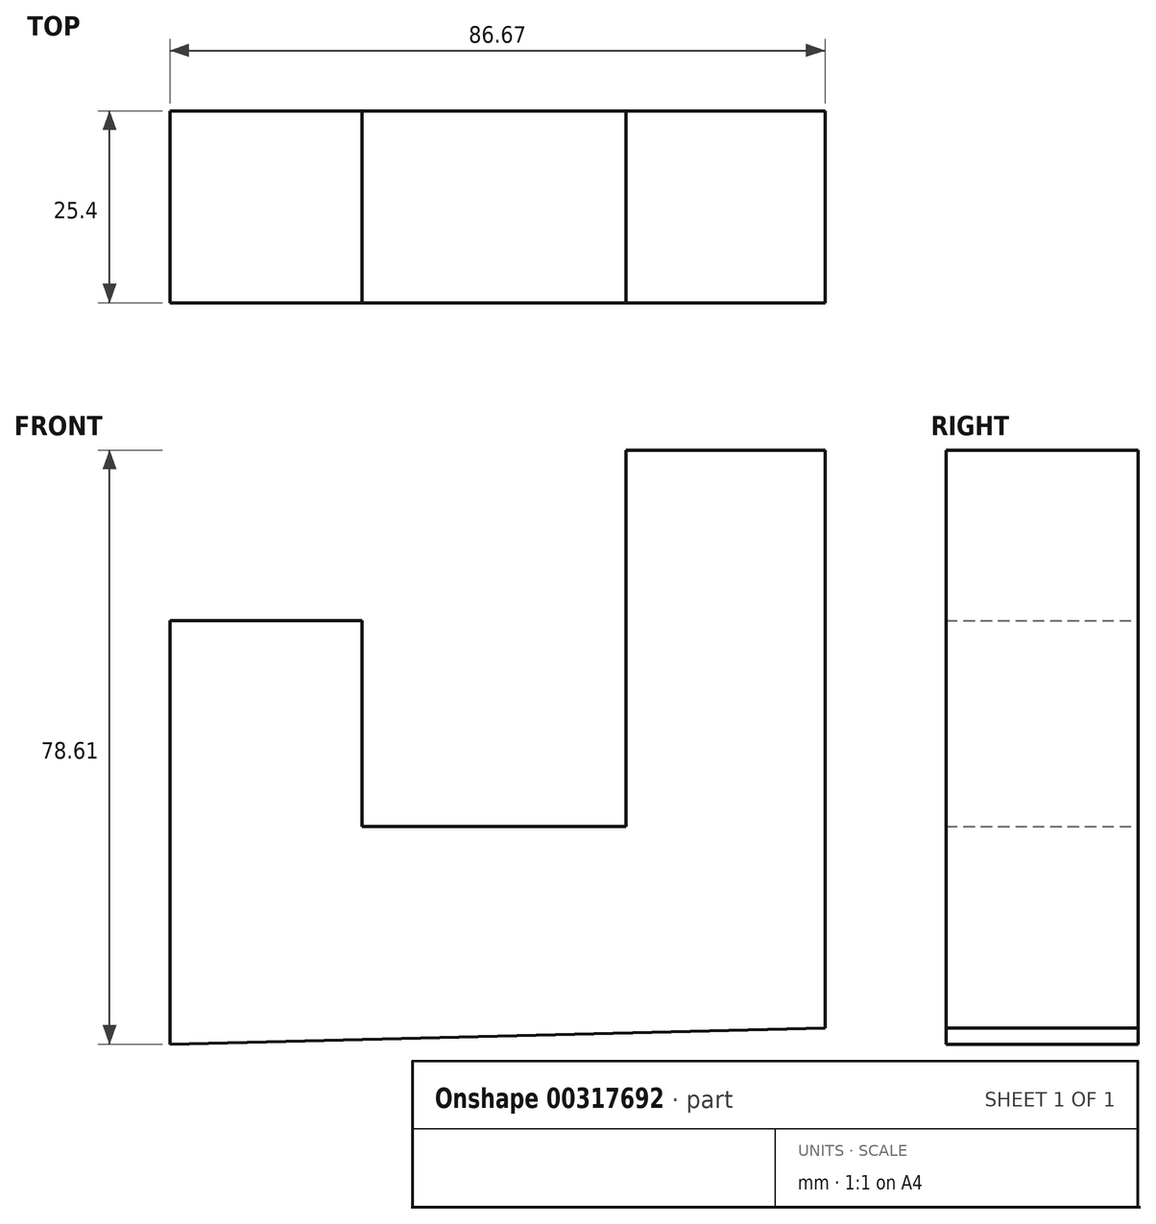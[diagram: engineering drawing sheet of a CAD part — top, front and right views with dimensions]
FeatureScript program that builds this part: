
annotation { "Feature Type Name" : "Feature", "Feature Type Description" : "" }
export const myFeature = defineFeature(function(context is Context, id is Id, definition is map)
    precondition{}
    {
        {
            var Q0;
            Q0=qCreatedBy(makeId("Front.planeOp"),FACE);
            var sketch = newSketch(context, id + "F0", { "sketchPlane" : qUnion([Q0])});
            skLineSegment(sketch, "E0", {"start": v(-46.12, -12.84) * mm, "end": v(-46.12, 15.94) * mm});
            skLineSegment(sketch, "E1", {"start": v(-46.12, 15.94) * mm, "end": v(-20.74, 15.94) * mm});
            skLineSegment(sketch, "E2", {"start": v(-20.74, 15.94) * mm, "end": v(-20.74, -11.3) * mm});
            skLineSegment(sketch, "E3", {"start": v(-20.74, -11.3) * mm, "end": v(14.24, -11.3) * mm});
            skLineSegment(sketch, "E4", {"start": v(14.24, -11.3) * mm, "end": v(14.24, 38.53) * mm});
            skLineSegment(sketch, "E5", {"start": v(14.24, 38.53) * mm, "end": v(40.55, 38.53) * mm});
            skLineSegment(sketch, "E6", {"start": v(40.55, 38.53) * mm, "end": v(40.55, -37.92) * mm});
            skLineSegment(sketch, "E7", {"start": v(40.55, -37.92) * mm, "end": v(-46.12, -40.08) * mm});
            skLineSegment(sketch, "E8", {"start": v(-46.12, -40.08) * mm, "end": v(-46.12, -12.84) * mm});
            skSolve(sketch);
        }
        {
            var Q0;
            Q0=makeQuery(id+"F0.imprint","IMPRINT",FACE,{"disambiguationData":[TD([[makeQuery(id+"F0.imprint","IMPRINT",EDGE,{"derivedFrom":sQuery(id+"F0.wireOp",EDGE,"E0")}),-1.0]])]});
            extrude(context, id + "F1", {"entities" : qUnion([Q0]), "depth" : 25.4 * mm});
        }
    });
